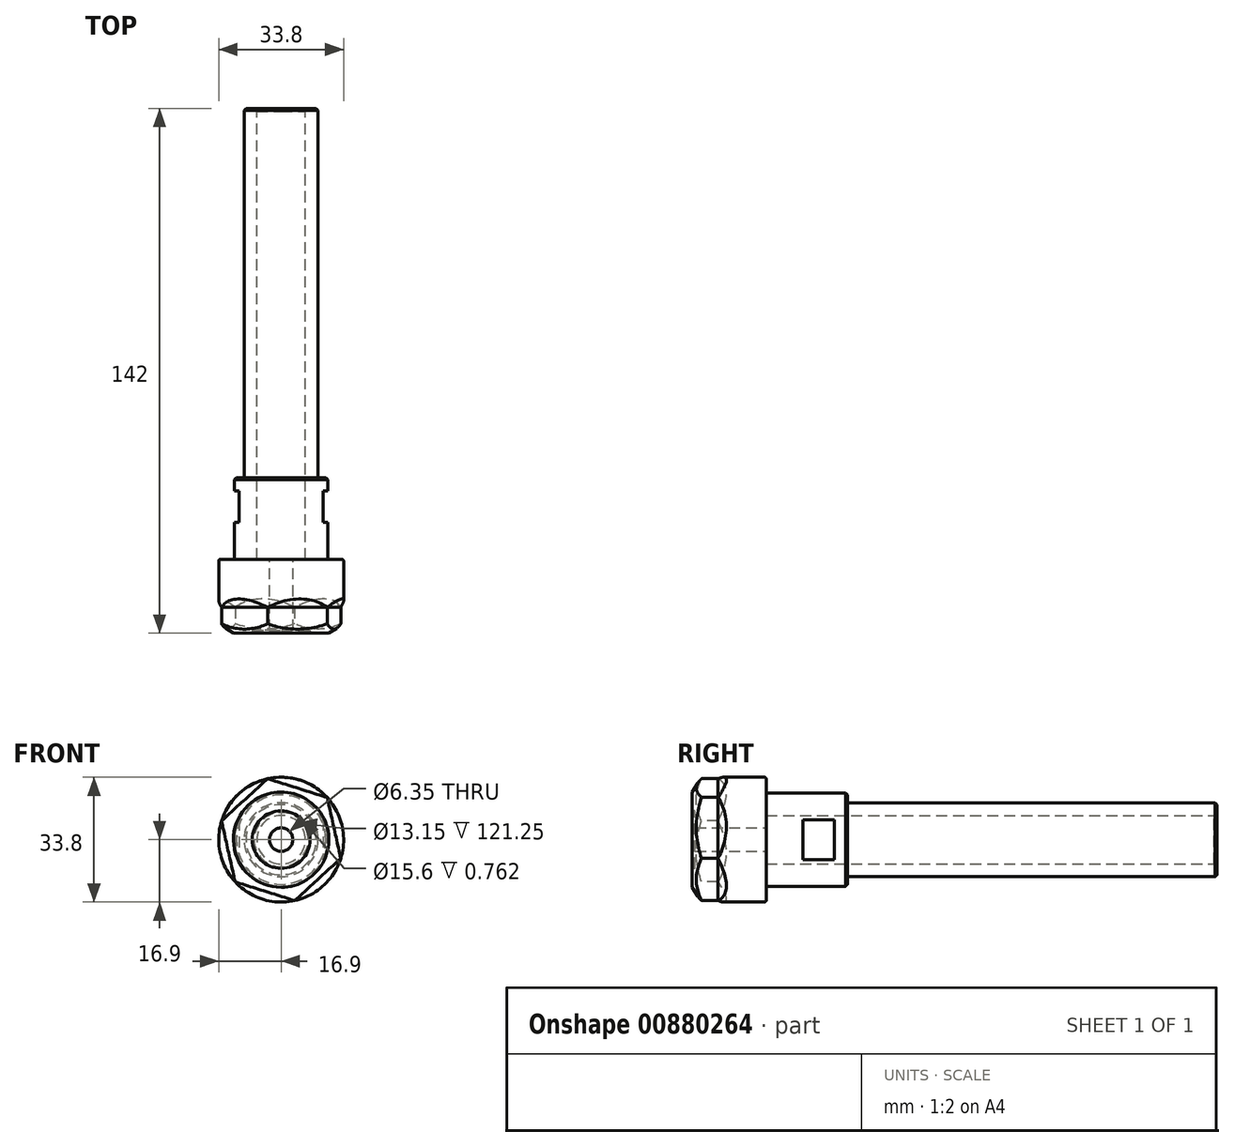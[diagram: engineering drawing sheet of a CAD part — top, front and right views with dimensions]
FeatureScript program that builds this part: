
annotation { "Feature Type Name" : "Feature", "Feature Type Description" : "" }
export const myFeature = defineFeature(function(context is Context, id is Id, definition is map)
    precondition{}
    {
        {
            var Q0;
            Q0=qCreatedBy(makeId("Front.planeOp"),FACE);
            var sketch = newSketch(context, id + "F0", { "sketchPlane" : qUnion([Q0])});
            skCircle(sketch, "E0", {"center": v(0, 0) * mm, "radius": 10 * mm});
            skCircle(sketch, "E1", {"center": v(0, 0) * mm, "radius": 6.58 * mm});
            skSolve(sketch);
        }
        {
            var Q0;
            Q0=qSketchRegion(id+"F0",true);
            extrude(context, id + "F1", {"entities" : qUnion([Q0]), "depth" : 100 * mm});
        }
        {
            var Q0;
            Q0=makeQuery(id+"F1.opExtrude","CAP_FACE",FACE,{"disambiguationData":[OSD([sQuery(id+"F0.wireOp",EDGE,"E0"),sQuery(id+"F0.wireOp",EDGE,"E1")])],"isStart":false});
            var sketch = newSketch(context, id + "F2", { "sketchPlane" : qUnion([Q0])});
            skCircle(sketch, "E2", {"center": v(0, 0) * mm, "radius": 12.6 * mm});
            skCircle(sketch, "E3", {"center": v(0, 0) * mm, "radius": 6.58 * mm});
            skSolve(sketch);
        }
        {
            var Q0;
            Q0=qSketchRegion(id+"F2",true);
            extrude(context, id + "F3", {"entities" : qUnion([Q0]), "operationType" : NewBodyOperationType.ADD, "depth" : 22 * mm});
        }
        {
            var Q0;
            Q0=makeQuery(id+"F3.opExtrude","CAP_FACE",FACE,{"disambiguationData":[OSD([sQuery(id+"F2.wireOp",EDGE,"E2"),sQuery(id+"F2.wireOp",EDGE,"E3")])],"isStart":false});
            var sketch = newSketch(context, id + "F4", { "sketchPlane" : qUnion([Q0])});
            skCircle(sketch, "E4.0", {"center": v(0, 0) * mm, "radius": 3.18 * mm});
            skCircle(sketch, "E5", {"center": v(0, 0) * mm, "radius": 16.9 * mm});
            skSolve(sketch);
        }
        {
            var Q0;
            Q0=qSketchRegion(id+"F4",true);
            extrude(context, id + "F5", {"entities" : qUnion([Q0]), "operationType" : NewBodyOperationType.ADD, "depth" : 20 * mm});
        }
        {
            var Q0;
            Q0=makeQuery(id+"F5.opExtrude","CAP_FACE",FACE,{"disambiguationData":[OSD([sQuery(id+"F4.wireOp",EDGE,"E4.0"),sQuery(id+"F4.wireOp",EDGE,"E5")])],"isStart":false});
            var sketch = newSketch(context, id + "F6", { "sketchPlane" : qUnion([Q0])});
            skCircle(sketch, "E6", {"center": v(0, 0) * mm, "radius": 7.8 * mm});
            skSolve(sketch);
        }
        {
            var Q0;
            Q0=qSketchRegion(id+"F6",true);
            extrude(context, id + "F7", {"entities" : qUnion([Q0]), "operationType" : NewBodyOperationType.REMOVE, "oppositeDirection" : true, "depth" : 0.76 * mm});
        }
        {
            var Q0;
            Q0=makeQuery(id+"F5.opExtrude","CAP_EDGE",EDGE,{"disambiguationData":[OSD([sQuery(id+"F4.wireOp",EDGE,"E5")])],"isStart":false});
            chamfer(context, id + "F8", {"entities" : qUnion([Q0]), "chamferType" : ChamferType.TWO_OFFSETS, "width1" : 4 * mm, "oppositeDirection" : false, "width2" : 2.5 * mm, "tangentPropagation" : true});
        }
        {
            var Q0;
            Q0=makeQuery(id+"F5.opExtrude","CAP_FACE",FACE,{"disambiguationData":[OSD([sQuery(id+"F4.wireOp",EDGE,"E4.0"),sQuery(id+"F4.wireOp",EDGE,"E5")])],"isStart":false});
            var sketch = newSketch(context, id + "F9", { "sketchPlane" : qUnion([Q0])});
            skCircle(sketch, "E7.cCircle", {"center": v(0, 0) * mm, "radius": 16.9 * mm, "construction": true});
            skLineSegment(sketch, "E7.0", {"start": v(12.45, 11.43) * mm, "end": v(16.12, -5.07) * mm});
            skLineSegment(sketch, "E7.1", {"start": v(16.12, -5.07) * mm, "end": v(3.67, -16.5) * mm});
            skLineSegment(sketch, "E7.2", {"start": v(3.67, -16.5) * mm, "end": v(-12.45, -11.43) * mm});
            skLineSegment(sketch, "E7.3", {"start": v(-12.45, -11.43) * mm, "end": v(-16.12, 5.07) * mm});
            skLineSegment(sketch, "E7.4", {"start": v(-16.12, 5.07) * mm, "end": v(-3.67, 16.5) * mm});
            skLineSegment(sketch, "E7.5", {"start": v(-3.67, 16.5) * mm, "end": v(12.45, 11.43) * mm});
            skCircle(sketch, "E8", {"center": v(0, 0) * mm, "radius": 21.1 * mm});
            skSolve(sketch);
        }
        {
            var Q0;
            {var subQ0=sQuery(id+"F9.wireOp",EDGE,"E7.0");Q0=makeQuery(id+"F9.imprint","IMPRINT",FACE,{"disambiguationData":[TD([[makeQuery(id+"F9.imprint","IMPRINT",EDGE,{"derivedFrom":subQ0}),1.0]])]});}
            var Q1;
            {var subQ0=sQuery(id+"F9.wireOp",EDGE,"E7.5");Q1=makeQuery(id+"F9.imprint","IMPRINT",FACE,{"disambiguationData":[TD([[makeQuery(id+"F9.imprint","IMPRINT",EDGE,{"derivedFrom":subQ0}),1.0]])]});}
            var Q2;
            {var subQ0=sQuery(id+"F9.wireOp",EDGE,"E7.4");Q2=makeQuery(id+"F9.imprint","IMPRINT",FACE,{"disambiguationData":[TD([[makeQuery(id+"F9.imprint","IMPRINT",EDGE,{"derivedFrom":subQ0}),1.0]])]});}
            var Q3;
            {var subQ0=sQuery(id+"F9.wireOp",EDGE,"E7.3");Q3=makeQuery(id+"F9.imprint","IMPRINT",FACE,{"disambiguationData":[TD([[makeQuery(id+"F9.imprint","IMPRINT",EDGE,{"derivedFrom":subQ0}),1.0]])]});}
            var Q4;
            {var subQ0=sQuery(id+"F9.wireOp",EDGE,"E7.2");Q4=makeQuery(id+"F9.imprint","IMPRINT",FACE,{"disambiguationData":[TD([[makeQuery(id+"F9.imprint","IMPRINT",EDGE,{"derivedFrom":subQ0}),1.0]])]});}
            var Q5;
            {var subQ0=sQuery(id+"F9.wireOp",EDGE,"E7.1");Q5=makeQuery(id+"F9.imprint","IMPRINT",FACE,{"disambiguationData":[TD([[makeQuery(id+"F9.imprint","IMPRINT",EDGE,{"derivedFrom":subQ0}),1.0]])]});}
            var Q6;
            Q6=makeQuery(id+"F9.imprint","IMPRINT",FACE,{"disambiguationData":[TD([[makeQuery(id+"F9.imprint","IMPRINT",EDGE,{"derivedFrom":sQuery(id+"F9.wireOp",EDGE,"E8")}),1.0]])]});
            extrude(context, id + "F10", {"entities" : qUnion([Q0, Q1, Q2, Q3, Q4, Q5, Q6]), "operationType" : NewBodyOperationType.REMOVE, "oppositeDirection" : true, "depth" : 10 * mm});
        }
        {
            var Q0;
            Q0=makeQuery(id+"F10.boolean.opBoolean","COPY",EDGE,{"derivedFrom":makeQuery(id+"F10.opExtrude","CAP_EDGE",EDGE,{"disambiguationData":[OSD([sQuery(id+"F9.wireOp",EDGE,"E7.5")])],"isStart":false})});
            chamfer(context, id + "F11", {"entities" : qUnion([Q0]), "width" : 3 * mm, "tangentPropagation" : true});
        }
        {
            var Q0;
            Q0=makeQuery(id+"F10.boolean.opBoolean","COPY",EDGE,{"derivedFrom":makeQuery(id+"F10.opExtrude","CAP_EDGE",EDGE,{"disambiguationData":[OSD([sQuery(id+"F9.wireOp",EDGE,"E7.4")])],"isStart":false})});
            chamfer(context, id + "F12", {"entities" : qUnion([Q0]), "width" : 3 * mm, "tangentPropagation" : true});
        }
        {
            var Q0;
            Q0=makeQuery(id+"F10.boolean.opBoolean","COPY",EDGE,{"derivedFrom":makeQuery(id+"F10.opExtrude","CAP_EDGE",EDGE,{"disambiguationData":[OSD([sQuery(id+"F9.wireOp",EDGE,"E7.3")])],"isStart":false})});
            chamfer(context, id + "F13", {"entities" : qUnion([Q0]), "width" : 3 * mm, "tangentPropagation" : true});
        }
        {
            var Q0;
            Q0=makeQuery(id+"F10.boolean.opBoolean","COPY",EDGE,{"derivedFrom":makeQuery(id+"F10.opExtrude","CAP_EDGE",EDGE,{"disambiguationData":[OSD([sQuery(id+"F9.wireOp",EDGE,"E7.2")])],"isStart":false})});
            chamfer(context, id + "F14", {"entities" : qUnion([Q0]), "width" : 3 * mm, "tangentPropagation" : true});
        }
        {
            var Q0;
            Q0=makeQuery(id+"F10.boolean.opBoolean","COPY",EDGE,{"derivedFrom":makeQuery(id+"F10.opExtrude","CAP_EDGE",EDGE,{"disambiguationData":[OSD([sQuery(id+"F9.wireOp",EDGE,"E7.1")])],"isStart":false})});
            chamfer(context, id + "F15", {"entities" : qUnion([Q0]), "width" : 3 * mm, "tangentPropagation" : true});
        }
        {
            var Q0;
            Q0=makeQuery(id+"F10.boolean.opBoolean","COPY",EDGE,{"derivedFrom":makeQuery(id+"F10.opExtrude","CAP_EDGE",EDGE,{"disambiguationData":[OSD([sQuery(id+"F9.wireOp",EDGE,"E7.0")])],"isStart":false})});
            chamfer(context, id + "F16", {"entities" : qUnion([Q0]), "width" : 3 * mm, "tangentPropagation" : true});
        }
        {
            var Q0;
            Q0=makeQuery(id+"F5.opExtrude","CAP_EDGE",EDGE,{"disambiguationData":[OSD([sQuery(id+"F4.wireOp",EDGE,"E5")])],"isStart":true});
            fillet(context, id + "F17", {"entities" : qUnion([Q0]), "radius" : .5 * mm, "tangentPropagation" : true, "allowEdgeOverflow" : false});
        }
        {
            var Q0;
            Q0=makeQuery(id+"F3.opExtrude","CAP_EDGE",EDGE,{"disambiguationData":[OSD([sQuery(id+"F2.wireOp",EDGE,"E2")])],"isStart":true});
            chamfer(context, id + "F18", {"entities" : qUnion([Q0]), "width" : .5 * mm, "tangentPropagation" : true});
        }
        {
            var Q0;
            Q0=qCreatedBy(makeId("Top.planeOp"),FACE);
            var sketch = newSketch(context, id + "F19", { "sketchPlane" : qUnion([Q0])});
            skLineSegment(sketch, "E9.bottom", {"start": v(11.37, -103.5) * mm, "end": v(15.01, -103.5) * mm});
            skLineSegment(sketch, "E9.top", {"start": v(11.37, -112) * mm, "end": v(15.01, -112) * mm});
            skLineSegment(sketch, "E9.left", {"start": v(11.37, -112) * mm, "end": v(11.37, -103.5) * mm});
            skLineSegment(sketch, "E9.right", {"start": v(15.01, -112) * mm, "end": v(15.01, -103.5) * mm});
            skLineSegment(sketch, "E10.bottom", {"start": v(-15.01, -103.5) * mm, "end": v(-11.37, -103.5) * mm});
            skLineSegment(sketch, "E10.top", {"start": v(-15.01, -112) * mm, "end": v(-11.37, -112) * mm});
            skLineSegment(sketch, "E10.left", {"start": v(-15.01, -112) * mm, "end": v(-15.01, -103.5) * mm});
            skLineSegment(sketch, "E10.right", {"start": v(-11.37, -112) * mm, "end": v(-11.37, -103.5) * mm});
            skLineSegment(sketch, "E11", {"start": v(0, -107.75) * mm, "end": v(11.37, -107.75) * mm, "construction": true});
            skLineSegment(sketch, "E12", {"start": v(0, -107.75) * mm, "end": v(-11.37, -107.75) * mm, "construction": true});
            skSolve(sketch);
        }
        {
            var Q0;
            Q0=qSketchRegion(id+"F19",true);
            extrude(context, id + "F20", {"entities" : qUnion([Q0]), "operationType" : NewBodyOperationType.REMOVE, "endBound" : BoundingType.THROUGH_ALL, "depth" : 25.4 * mm, "hasSecondDirection" : true, "secondDirectionBound" : BoundingType.THROUGH_ALL, "secondDirectionOppositeDirection" : true, "secondDirectionDepth" : 25.4 * mm});
        }
        {
            var Q0;
            Q0=makeQuery(id+"F1.opExtrude","CAP_EDGE",EDGE,{"disambiguationData":[OSD([sQuery(id+"F0.wireOp",EDGE,"E1")])],"isStart":true});
            chamfer(context, id + "F21", {"entities" : qUnion([Q0]), "width" : .75 * mm, "tangentPropagation" : true});
        }
        {
            var Q0;
            Q0=makeQuery(id+"F1.opExtrude","CAP_EDGE",EDGE,{"disambiguationData":[OSD([sQuery(id+"F0.wireOp",EDGE,"E0")])],"isStart":true});
            chamfer(context, id + "F22", {"entities" : qUnion([Q0]), "width" : .5 * mm, "tangentPropagation" : true});
        }
    });
